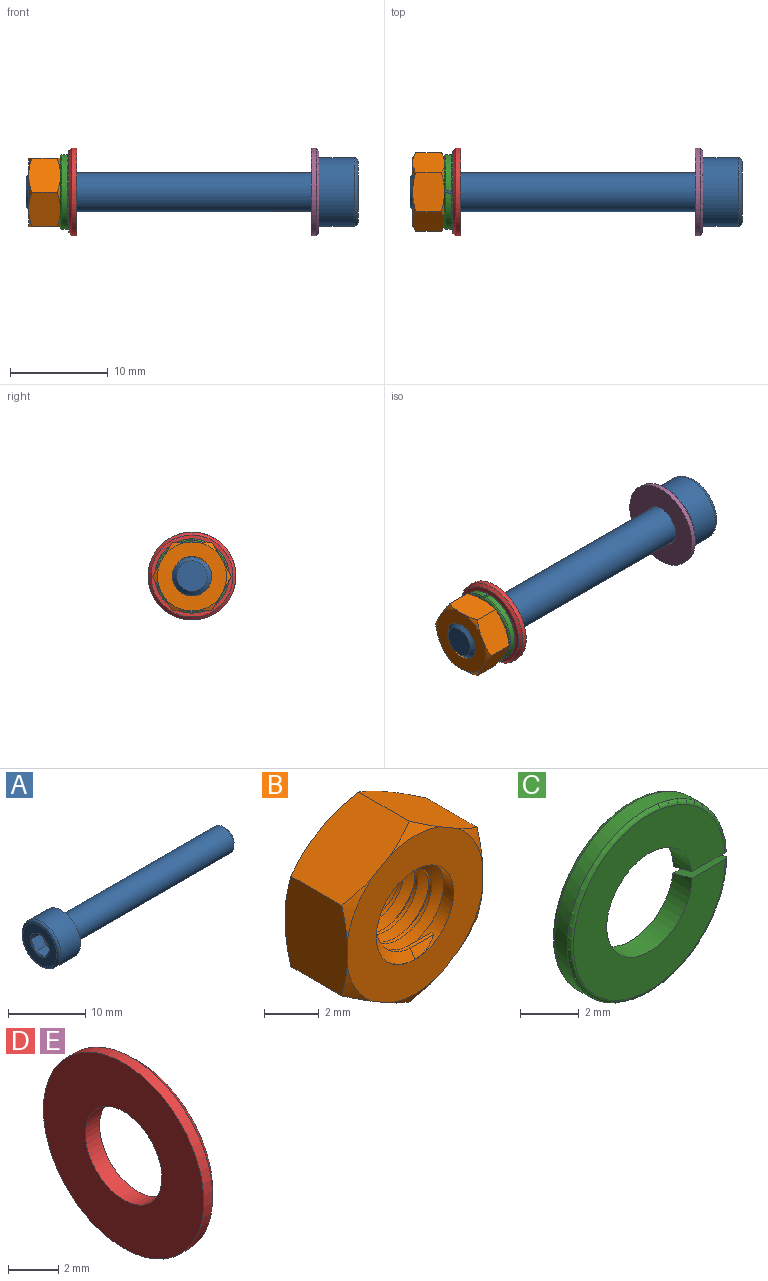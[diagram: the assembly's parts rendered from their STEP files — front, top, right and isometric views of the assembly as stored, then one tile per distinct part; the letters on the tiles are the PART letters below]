
ASSEMBLY  parts=5 mates=4
PART A: 24 faces, bbox 34x7.6x7.6 mm
  f0: plane 1.3x0.75mm, normal (-1,0,0), area 0.1mm2, adj f16,f17,f23
  f1: plane 1.5x0.43mm, normal (-1,0,0), area 0.1mm2, adj f17,f18,f23
  f2: plane 1.3x0.75mm, normal (-1,0,0), area 0.1mm2, adj f18,f19,f23
  f3: plane 1.3x0.75mm, normal (-1,0,0), area 0.1mm2, adj f19,f20,f23
  f4: plane 1.5x0.43mm, normal (-1,0,0), area 0.1mm2, adj f20,f21,f23
  f5: cone r=1.74mm half-angle=60deg, axis (-1,0,0), area 2mm2, adj f15,f16,f17,f18,f19,f20,f21
  f6: cone r=2.01mm half-angle=20.6deg, axis (-1,0,0), area 5.6mm2, adj f7,f11
  f7: torus R=2.2mm, axis (1,0,0), area 0.9mm2, adj f6,f10
  f8: plane 3.14x3.14mm, normal (1,0,0), area 7.7mm2, adj f9
  f9: cone r=2mm half-angle=45deg, axis (-1,0,0), area 6.8mm2, adj f8,f10
  f10: cylinder r=2mm len=28.97mm, axis (1,0,0), area 364.1mm2, adj f7,f9
  f11: torus R=2.35mm, axis (1,0,0), area 3.4mm2, adj f6,f13
  f12: cylinder r=3.5mm len=7mm, axis (1,0,0), area 79.2mm2, adj f13,f14
  f13: plane 7x7mm, normal (1,0,0), area 21.1mm2, adj f11,f12
  f14: torus R=3.1mm, axis (1,0,0), area 13.2mm2, adj f12,f15
  f15: plane 6.2x6.2mm, normal (-1,0,0), area 20.7mm2, adj f5,f14
  f16: plane 2x1.74mm, normal (0,0,-1), area 3.3mm2, adj f0,f5,f17,f21,f22
  f17: plane 2x1.5mm, normal (0,0.87,-0.5), area 3.3mm2, adj f0,f1,f5,f16,f18
  f18: plane 2x1.5mm, normal (0,0.87,0.5), area 3.3mm2, adj f1,f2,f5,f17,f19
  f19: plane 2x1.74mm, normal (0,0,1), area 3.3mm2, adj f2,f3,f5,f18,f20
  f20: plane 2x1.5mm, normal (0,-0.87,0.5), area 3.3mm2, adj f3,f4,f5,f19,f21
  f21: plane 2x1.5mm, normal (0,-0.87,-0.5), area 3.3mm2, adj f4,f5,f16,f20,f22
  f22: plane 1.3x0.75mm, normal (-1,0,0), area 0.1mm2, adj f16,f21,f23
  f23: cone r=1.5mm half-angle=60deg, axis (-1,0,0), area 8.2mm2, adj f0,f1,f2,f3,f4,f22
PART B: 28 faces, bbox 8.2x3.5x8.3 mm
  f0: cone r=3.54mm half-angle=60deg, axis (0,-1,0), area 0.8mm2, adj f11,f22,f23
  f1: cone r=3.54mm half-angle=60deg, axis (0,-1,0), area 0.8mm2, adj f11,f23,f24
  f2: cone r=3.54mm half-angle=60deg, axis (0,-1,0), area 0.8mm2, adj f11,f24,f25
  f3: cone r=3.54mm half-angle=60deg, axis (0,-1,0), area 0.8mm2, adj f11,f25,f26
  f4: cone r=3.54mm half-angle=60deg, axis (0,-1,0), area 0.8mm2, adj f11,f22,f27
  f5: cone r=4.04mm half-angle=60deg, axis (0,1,0), area 0.8mm2, adj f10,f22,f23
  f6: cone r=4.04mm half-angle=60deg, axis (0,1,0), area 0.8mm2, adj f10,f23,f24
  f7: cone r=4.04mm half-angle=60deg, axis (0,1,0), area 0.8mm2, adj f10,f24,f25
  f8: cone r=4.04mm half-angle=60deg, axis (0,1,0), area 0.8mm2, adj f10,f25,f26
  f9: cone r=4.04mm half-angle=60deg, axis (0,1,0), area 0.8mm2, adj f10,f26,f27
  f10: plane 7.08x7mm, normal (0,-1,0), area 26.7mm2, adj f5,f6,f7,f8,f9,f12,f21,f22
  f11: plane 7.08x7mm, normal (0,1,0), area 26.7mm2, adj f0,f1,f2,f3,f4,f12,f20,f22
  f12: cylinder r=2mm len=4mm, axis (0,1,0), area 11.1mm2, adj f10,f11,f13,f15,f16,f17,f18,f19
  f13: plane 0.62x0.38mm, normal (0.35,0,-0.94), area 0.2mm2, adj f12,f14,f15,f16
  f14: cylinder r=1.6mm len=3.2mm, axis (0,1,0), area 5.7mm2, adj f13,f15,f16,f17
  f15: bspline ~4.62x4mm, area 19.3mm2, adj f12,f13,f14,f18
  f16: bspline ~4.62x4mm, area 19.3mm2, adj f12,f13,f14,f19
  f17: plane 1.2x0.15mm, normal (0,0,1), area 0.2mm2, adj f12,f14,f18,f19
  f18: plane 1.31x0.51mm, normal (0,0.87,0.5), area 0.4mm2, adj f12,f15,f17
  f19: plane 1.31x0.51mm, normal (0,-0.87,0.5), area 0.4mm2, adj f12,f16,f17
  f20: cone r=3.54mm half-angle=60deg, axis (0,-1,0), area 0.8mm2, adj f11,f26,f27
  f21: cone r=4.04mm half-angle=60deg, axis (0,1,0), area 0.8mm2, adj f10,f22,f27
  f22: plane 3.68x3.38mm, normal (-0.5,0,0.87), area 12.2mm2, adj f0,f4,f5,f10,f11,f21,f23,f27
  f23: plane 3.68x3.38mm, normal (0.5,0,0.87), area 12.2mm2, adj f0,f1,f5,f6,f10,f11,f22,f24
  f24: plane 4.23x3.38mm, normal (1,0,0), area 12.2mm2, adj f1,f2,f6,f7,f10,f11,f23,f25
  f25: plane 3.68x3.38mm, normal (0.5,0,-0.87), area 12.2mm2, adj f2,f3,f7,f8,f10,f11,f24,f26
  f26: plane 3.68x3.38mm, normal (-0.5,0,-0.87), area 12.2mm2, adj f3,f8,f9,f10,f11,f20,f25,f27
  f27: plane 4.23x3.38mm, normal (-1,0,0), area 12.2mm2, adj f4,f9,f10,f11,f20,f21,f22,f26
PART C: 8 faces, bbox 8.2x0.9x8.2 mm
  f0: cylinder r=2.05mm len=4.1mm, axis (0,1,0), area 11.3mm2, adj f2,f3,f4,f5
  f1: cylinder r=3.8mm len=7.6mm, axis (0,1,0), area 14.2mm2, adj f4,f5,f6,f7
  f2: plane 7.3x7.3mm, normal (0,-1,0), area 28.2mm2, adj f0,f4,f5,f6
  f3: plane 7.3x7.3mm, normal (0,1,0), area 28.2mm2, adj f0,f4,f5,f7
  f4: plane 1.78x0.92mm, normal (0,-0.26,-0.97), area 1.6mm2, adj f0,f1,f2,f3,f6,f7
  f5: plane 1.78x0.92mm, normal (0,0.26,0.97), area 1.6mm2, adj f0,f1,f2,f3,f6,f7
  f6: torus R=3.65mm, axis (0,1,0), area 5.5mm2, adj f1,f2,f4,f5
  f7: torus R=3.65mm, axis (0,1,0), area 5.5mm2, adj f1,f3,f4,f5
PART D: 5 faces, bbox 0.8x9x9 mm
  f0: plane 9x9mm, normal (-1,0,0), area 49.1mm2, adj f1,f4
  f1: cylinder r=2.15mm len=4.3mm, axis (1,0,0), area 10.8mm2, adj f0,f2
  f2: plane 8.4x8.4mm, normal (1,0,0), area 40.9mm2, adj f1,f3
  f3: cone r=4.2mm half-angle=45deg, axis (-1,0,0), area 11.6mm2, adj f2,f4
  f4: cylinder r=4.5mm len=9mm, axis (1,0,0), area 14.1mm2, adj f0,f3
PART E: same geometry as D
PLACE A rot(axis=(0,1,0),180deg) t=(0.8,0,0)mm
PLACE B rot(axis=(0.58,-0.58,0.58),120deg) t=(-28.9,0,-0.04)mm
PLACE C rot(axis=(0.58,-0.58,0.58),120deg) t=(-25.7,0,0)mm
PLACE D rot(axis=(0,-0.71,-0.71),180deg) t=(-24,0,0)mm
PLACE E at identity fixed
MATE fastened D.f1 <-> E.f1  axis (1,0,0) through (-22,0,0)mm
MATE fastened A.f5 <-> E.f1  axis (-1,0,0) through (0.8,0,0)mm
MATE fastened B.f0 <-> C.f3  axis (1,0,0) through (-25.7,0,-0.04)mm
MATE fastened C.f0 <-> D.f1  axis (1,0,0) through (-24.8,0,0)mm
